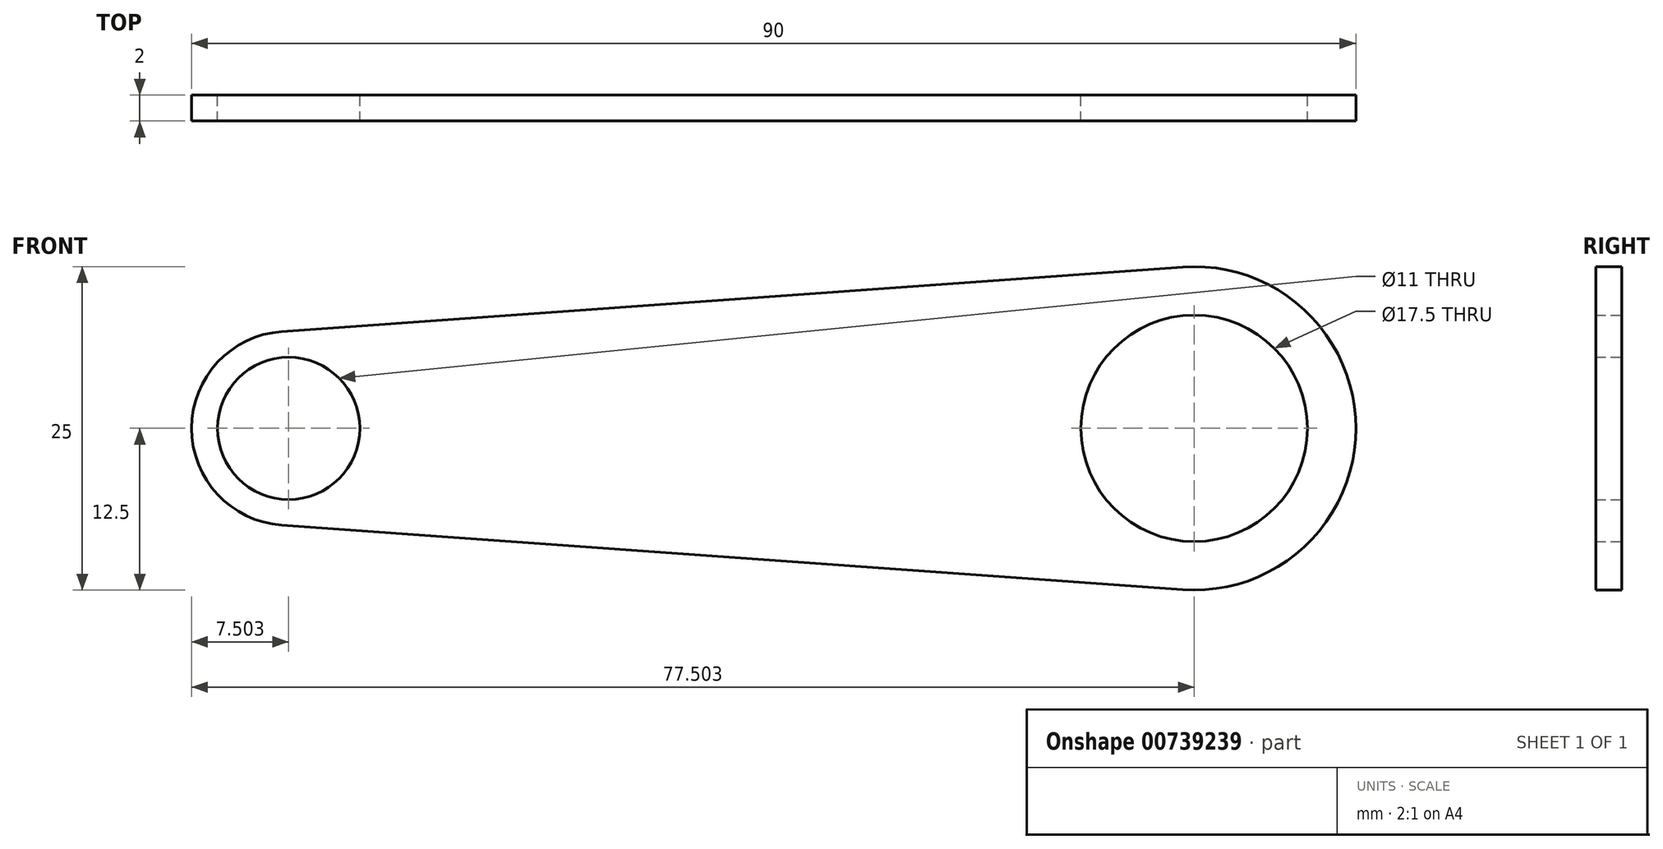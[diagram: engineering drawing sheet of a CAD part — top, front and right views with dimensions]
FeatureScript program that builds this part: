
annotation { "Feature Type Name" : "Feature", "Feature Type Description" : "" }
export const myFeature = defineFeature(function(context is Context, id is Id, definition is map)
    precondition{}
    {
        {
            var Q0;
            Q0=qCreatedBy(makeId("Front.planeOp"),FACE);
            var sketch = newSketch(context, id + "F0", { "sketchPlane" : qUnion([Q0])});
            skCircle(sketch, "E0", {"center": v(-1.97, 0) * mm, "radius": 7.5 * mm});
            skCircle(sketch, "E1", {"center": v(68.03, 0) * mm, "radius": 12.5 * mm});
            skLineSegment(sketch, "E2", {"start": v(-2.5, 7.48) * mm, "end": v(67.14, 12.47) * mm});
            skLineSegment(sketch, "E3", {"start": v(67.14, -12.47) * mm, "end": v(-2.5, -7.48) * mm});
            skCircle(sketch, "E4", {"center": v(-1.97, 0) * mm, "radius": 5.5 * mm});
            skCircle(sketch, "E5", {"center": v(68.03, 0) * mm, "radius": 8.75 * mm});
            skSolve(sketch);
        }
        {
            var Q0;
            Q0 = qSketchRegion(id + "F0", true);
            extrude(context, id + "F1", {"entities" : qUnion([Q0]), "depth" : 2 * mm, "offsetDistance" : 25.4 * mm});
        }
    });
